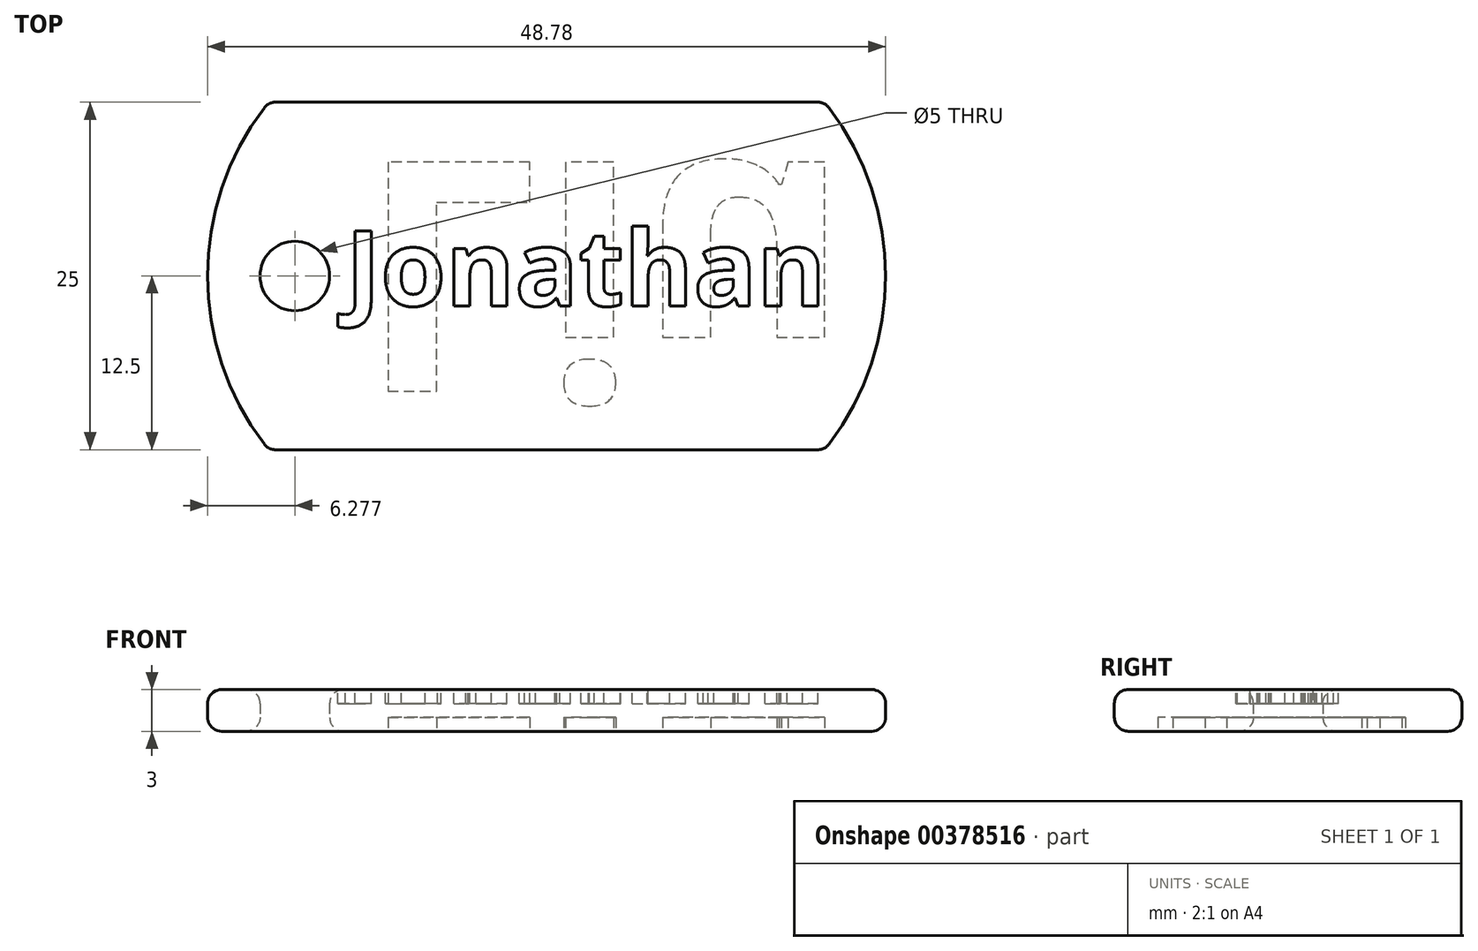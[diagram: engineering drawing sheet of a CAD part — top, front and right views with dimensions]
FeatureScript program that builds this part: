
annotation { "Feature Type Name" : "Feature", "Feature Type Description" : "" }
export const myFeature = defineFeature(function(context is Context, id is Id, definition is map)
    precondition{}
    {
        {
            var Q0;
            Q0=qCreatedBy(makeId("Top.planeOp"),FACE);
            var sketch = newSketch(context, id + "F0", { "sketchPlane" : qUnion([Q0])});
            skLineSegment(sketch, "E0.bottom", {"start": v(-20, 12.5) * mm, "end": v(20, 12.5) * mm});
            skLineSegment(sketch, "E0.top", {"start": v(-20, -12.5) * mm, "end": v(20, -12.5) * mm});
            skArc(sketch, "E1", {"start": v(-20, 12.5) * mm, "mid": v(-24.39, 0) * mm, "end": v(-20, -12.5) * mm});
            skArc(sketch, "E2", {"start": v(20, -12.5) * mm, "mid": v(24.39, 0) * mm, "end": v(20, 12.5) * mm});
            skCircle(sketch, "E3", {"center": v(-18.11, 0) * mm, "radius": 2.5 * mm});
            skSolve(sketch);
        }
        {
            var Q0;
            Q0=makeQuery(id+"F0.imprint","IMPRINT",FACE,{"disambiguationData":[TD([[makeQuery(id+"F0.imprint","IMPRINT",EDGE,{"derivedFrom":sQuery(id+"F0.wireOp",EDGE,"E0.bottom")}),-1.0]])]});
            extrude(context, id + "F1", {"entities" : qUnion([Q0]), "depth" : 3 * mm});
        }
        {
            var Q0;
            Q0=makeQuery(id+"F1.opExtrude","CAP_FACE",FACE,{"disambiguationData":[OSD([sQuery(id+"F0.wireOp",EDGE,"E0.bottom"),sQuery(id+"F0.wireOp",EDGE,"E0.top"),sQuery(id+"F0.wireOp",EDGE,"E1"),sQuery(id+"F0.wireOp",EDGE,"E2"),sQuery(id+"F0.wireOp",EDGE,"E3")])],"isStart":false});
            var sketch = newSketch(context, id + "F2", { "sketchPlane" : qUnion([Q0])});
            skText(sketch, "E4", { "text": "Jonathan", "fontName": "OpenSans-Bold.ttf"});
            const initialGuessF2  = {"E4": [-0.01445, -0.00215, 1, 0, 0.00545]};
            skSetInitialGuess(sketch, initialGuessF2);
            skSolve(sketch);
        }
        {
            var Q0;
            Q0=qSketchRegion(id+"F2",true);
            extrude(context, id + "F3", {"entities" : qUnion([Q0]), "operationType" : NewBodyOperationType.REMOVE, "oppositeDirection" : true, "depth" : 1 * mm});
        }
        {
            var Q0;
            Q0=makeQuery(id+"F1.opExtrude","CAP_FACE",FACE,{"disambiguationData":[OSD([sQuery(id+"F0.wireOp",EDGE,"E0.bottom"),sQuery(id+"F0.wireOp",EDGE,"E0.top"),sQuery(id+"F0.wireOp",EDGE,"E1"),sQuery(id+"F0.wireOp",EDGE,"E2"),sQuery(id+"F0.wireOp",EDGE,"E3")])],"isStart":true});
            var sketch = newSketch(context, id + "F4", { "sketchPlane" : qUnion([Q0])});
            skText(sketch, "E5", { "text": "Liu", "fontName": "OpenSans-Bold.ttf"});
            const initialGuessF4  = {"E5": [-0.01349, -0.0082, 1, 0, 0.01664]};
            skSetInitialGuess(sketch, initialGuessF4);
            skSolve(sketch);
        }
        {
            var Q0;
            Q0=qSketchRegion(id+"F4",true);
            extrude(context, id + "F5", {"entities" : qUnion([Q0]), "operationType" : NewBodyOperationType.REMOVE, "oppositeDirection" : true, "depth" : 1 * mm});
        }
        {
            var Q0;
            Q0=makeQuery(id+"F1.opExtrude","SWEPT_FACE",FACE,{"disambiguationData":[OSD([sQuery(id+"F0.wireOp",EDGE,"E2")])]});
            var Q1;
            Q1=makeQuery(id+"F1.opExtrude","SWEPT_FACE",FACE,{"disambiguationData":[OSD([sQuery(id+"F0.wireOp",EDGE,"E0.top")])]});
            var Q2;
            Q2=makeQuery(id+"F1.opExtrude","SWEPT_FACE",FACE,{"disambiguationData":[OSD([sQuery(id+"F0.wireOp",EDGE,"E3")])]});
            var Q3;
            Q3=makeQuery(id+"F1.opExtrude","SWEPT_FACE",FACE,{"disambiguationData":[OSD([sQuery(id+"F0.wireOp",EDGE,"E1")])]});
            var Q4;
            Q4=makeQuery(id+"F1.opExtrude","SWEPT_FACE",FACE,{"disambiguationData":[OSD([sQuery(id+"F0.wireOp",EDGE,"E0.bottom")])]});
            fillet(context, id + "F6", {"entities" : qUnion([Q0, Q1, Q2, Q3, Q4]), "radius" : 1 * mm, "tangentPropagation" : true, "allowEdgeOverflow" : false});
        }
    });
